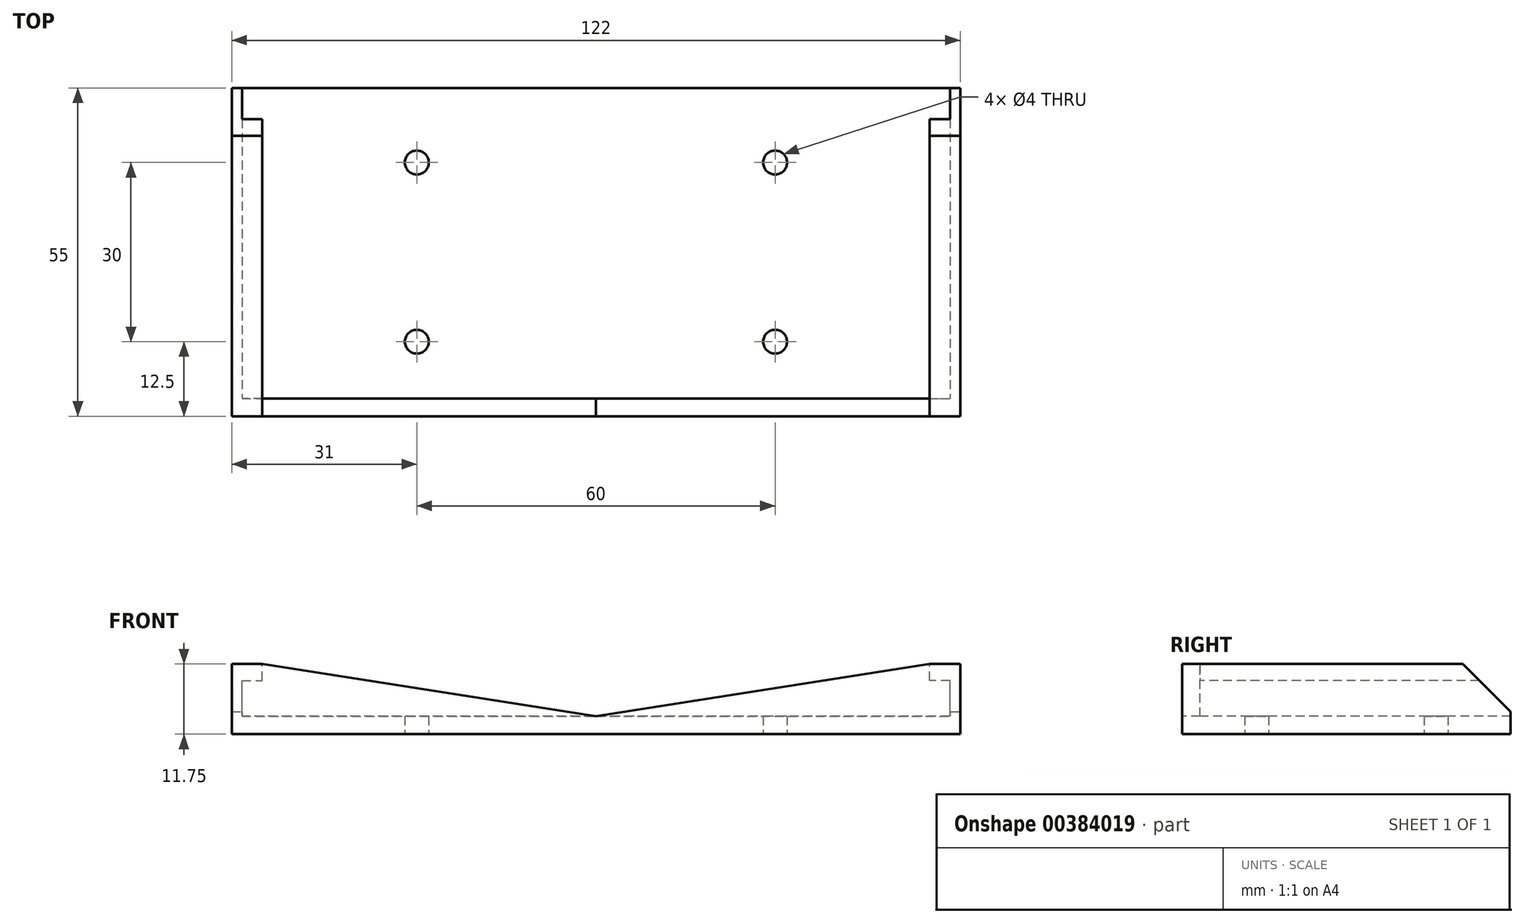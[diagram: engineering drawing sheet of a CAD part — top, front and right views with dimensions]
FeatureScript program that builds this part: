
annotation { "Feature Type Name" : "Feature", "Feature Type Description" : "" }
export const myFeature = defineFeature(function(context is Context, id is Id, definition is map)
    precondition{}
    {
        {
            var Q0;
            Q0=qCreatedBy(makeId("Top.planeOp"),FACE);
            var sketch = newSketch(context, id + "F0", { "sketchPlane" : qUnion([Q0])});
            skLineSegment(sketch, "E0.bottom", {"start": v(60, -27.5) * mm, "end": v(-60, -27.5) * mm});
            skLineSegment(sketch, "E0.top", {"start": v(60, 27.5) * mm, "end": v(-60, 27.5) * mm});
            skLineSegment(sketch, "E0.left", {"start": v(60, -27.5) * mm, "end": v(60, 27.5) * mm});
            skLineSegment(sketch, "E0.right", {"start": v(-60, -27.5) * mm, "end": v(-60, 27.5) * mm});
            skPoint(sketch, "E0.middle", {"position": v(0, 0) * mm});
            skCircle(sketch, "E1", {"center": v(-30, 15) * mm, "radius": 2 * mm});
            skCircle(sketch, "E2", {"center": v(30, 15) * mm, "radius": 2 * mm});
            skCircle(sketch, "E3", {"center": v(30, -15) * mm, "radius": 2 * mm});
            skCircle(sketch, "E4", {"center": v(-30, -15) * mm, "radius": 2 * mm});
            skSolve(sketch);
        }
        {
            var Q0;
            Q0 = qSketchRegion(id + "F0", true);
            extrude(context, id + "F1", {"entities" : qUnion([Q0]), "depth" : 3 * mm});
        }
        {
            var Q0;
            Q0=makeQuery(id+"F1.opExtrude","CAP_FACE",FACE,{"disambiguationData":[OSD([sQuery(id+"F0.wireOp",EDGE,"E0.bottom"),sQuery(id+"F0.wireOp",EDGE,"E0.top"),sQuery(id+"F0.wireOp",EDGE,"E0.left"),sQuery(id+"F0.wireOp",EDGE,"E0.right"),sQuery(id+"F0.wireOp",EDGE,"E1"),sQuery(id+"F0.wireOp",EDGE,"E2"),sQuery(id+"F0.wireOp",EDGE,"E3"),sQuery(id+"F0.wireOp",EDGE,"E4")])],"isStart":false});
            var sketch = newSketch(context, id + "F2", { "sketchPlane" : qUnion([Q0])});
            skLineSegment(sketch, "E5", {"start": v(58.88, 27.5) * mm, "end": v(58.88, -27.5) * mm});
            skLineSegment(sketch, "E6", {"start": v(58.88, 27.5) * mm, "end": v(60, 27.5) * mm});
            skLineSegment(sketch, "E7", {"start": v(60, 27.5) * mm, "end": v(60, -27.5) * mm});
            skLineSegment(sketch, "E8", {"start": v(60, -27.5) * mm, "end": v(58.88, -27.5) * mm});
            skLineSegment(sketch, "E9.MirrorCS", {"start": v(-60, -27.5) * mm, "end": v(-58.88, -27.5) * mm});
            skLineSegment(sketch, "E10.MirrorCS", {"start": v(-58.88, 27.5) * mm, "end": v(-60, 27.5) * mm});
            skLineSegment(sketch, "E11.MirrorCS", {"start": v(-60, 27.5) * mm, "end": v(-60, -27.5) * mm});
            skLineSegment(sketch, "E12.MirrorCS", {"start": v(-58.88, 27.5) * mm, "end": v(-58.88, -27.5) * mm});
            skSolve(sketch);
        }
        {
            var Q0;
            Q0 = qSketchRegion(id + "F2", true);
            extrude(context, id + "F3", {"entities" : qUnion([Q0]), "operationType" : NewBodyOperationType.ADD, "depth" : 6 * mm});
        }
        {
            var Q0;
            Q0=makeQuery(id+"F3.boolean.opBoolean","MERGE",FACE,{"derivedFrom":[makeQuery(id+"F1.opExtrude","SWEPT_FACE",FACE,{"disambiguationData":[OSD([sQuery(id+"F0.wireOp",EDGE,"E0.bottom")])]}),makeQuery(id+"F3.opExtrude","SWEPT_FACE",FACE,{"disambiguationData":[OSD([sQuery(id+"F2.wireOp",EDGE,"E8")])]}),makeQuery(id+"F3.opExtrude","SWEPT_FACE",FACE,{"disambiguationData":[OSD([sQuery(id+"F2.wireOp",EDGE,"E9.MirrorCS")])]})]});
            var sketch = newSketch(context, id + "F4", { "sketchPlane" : qUnion([Q0])});
            skLineSegment(sketch, "E13", {"start": v(-58.88, 3) * mm, "end": v(-58.88, 9) * mm});
            skLineSegment(sketch, "E14", {"start": v(-58.88, 9) * mm, "end": v(-55.88, 9) * mm});
            skLineSegment(sketch, "E15", {"start": v(-55.88, 9) * mm, "end": v(-55.88, 11.75) * mm});
            skLineSegment(sketch, "E16", {"start": v(-55.88, 11.75) * mm, "end": v(-61.88, 11.75) * mm});
            skLineSegment(sketch, "E17", {"start": v(-61.88, 11.75) * mm, "end": v(-61.88, 0) * mm});
            skLineSegment(sketch, "E18", {"start": v(-61.88, 0) * mm, "end": v(-52.74, 0) * mm});
            skLineSegment(sketch, "E19", {"start": v(-52.74, 0) * mm, "end": v(-58.88, 3) * mm});
            skLineSegment(sketch, "E20.MirrorCS", {"start": v(55.88, 11.75) * mm, "end": v(61.88, 11.75) * mm});
            skLineSegment(sketch, "E21.MirrorCS", {"start": v(61.88, 11.75) * mm, "end": v(61.88, 0) * mm});
            skLineSegment(sketch, "E22.MirrorCS", {"start": v(61.88, 0) * mm, "end": v(52.74, 0) * mm});
            skLineSegment(sketch, "E23.MirrorCS", {"start": v(58.88, 3) * mm, "end": v(58.88, 9) * mm});
            skLineSegment(sketch, "E24.MirrorCS", {"start": v(55.88, 9) * mm, "end": v(55.88, 11.75) * mm});
            skLineSegment(sketch, "E25.MirrorCS", {"start": v(52.74, 0) * mm, "end": v(58.88, 3) * mm});
            skLineSegment(sketch, "E26.MirrorCS", {"start": v(58.88, 9) * mm, "end": v(55.88, 9) * mm});
            skSolve(sketch);
        }
        {
            var Q0;
            Q0 = qSketchRegion(id + "F4", true);
            extrude(context, id + "F5", {"entities" : qUnion([Q0]), "operationType" : NewBodyOperationType.ADD, "oppositeDirection" : true, "depth" : 55 * mm});
        }
        {
            var Q0;
            Q0=makeQuery(id+"F5.boolean.opBoolean","MERGE",FACE,{"derivedFrom":[makeQuery(id+"F3.boolean.opBoolean","MERGE",FACE,{"derivedFrom":[makeQuery(id+"F1.opExtrude","SWEPT_FACE",FACE,{"disambiguationData":[OSD([sQuery(id+"F0.wireOp",EDGE,"E0.bottom")])]}),makeQuery(id+"F3.opExtrude","SWEPT_FACE",FACE,{"disambiguationData":[OSD([sQuery(id+"F2.wireOp",EDGE,"E8")])]}),makeQuery(id+"F3.opExtrude","SWEPT_FACE",FACE,{"disambiguationData":[OSD([sQuery(id+"F2.wireOp",EDGE,"E9.MirrorCS")])]})]}),makeQuery(id+"F5.opExtrude","CAP_FACE",FACE,{"disambiguationData":[OSD([sQuery(id+"F4.wireOp",EDGE,"E13"),sQuery(id+"F4.wireOp",EDGE,"E14"),sQuery(id+"F4.wireOp",EDGE,"E15"),sQuery(id+"F4.wireOp",EDGE,"E16"),sQuery(id+"F4.wireOp",EDGE,"E17"),sQuery(id+"F4.wireOp",EDGE,"E18"),sQuery(id+"F4.wireOp",EDGE,"E19")])],"isStart":true}),makeQuery(id+"F5.opExtrude","CAP_FACE",FACE,{"disambiguationData":[OSD([sQuery(id+"F4.wireOp",EDGE,"E20.MirrorCS"),sQuery(id+"F4.wireOp",EDGE,"E21.MirrorCS"),sQuery(id+"F4.wireOp",EDGE,"E22.MirrorCS"),sQuery(id+"F4.wireOp",EDGE,"E23.MirrorCS"),sQuery(id+"F4.wireOp",EDGE,"E24.MirrorCS"),sQuery(id+"F4.wireOp",EDGE,"E25.MirrorCS"),sQuery(id+"F4.wireOp",EDGE,"E26.MirrorCS")])],"isStart":true})]});
            var sketch = newSketch(context, id + "F6", { "sketchPlane" : qUnion([Q0])});
            skLineSegment(sketch, "E27", {"start": v(-58.88, 9) * mm, "end": v(-59.27, 9) * mm});
            skLineSegment(sketch, "E28", {"start": v(-59.27, 9) * mm, "end": v(-59.27, 3) * mm});
            skLineSegment(sketch, "E29", {"start": v(-59.27, 3) * mm, "end": v(-58.88, 3) * mm});
            skLineSegment(sketch, "E30.MirrorCS", {"start": v(59.27, 3) * mm, "end": v(58.88, 3) * mm});
            skLineSegment(sketch, "E31.MirrorCS", {"start": v(59.27, 9) * mm, "end": v(59.27, 3) * mm});
            skLineSegment(sketch, "E32.MirrorCS", {"start": v(58.88, 9) * mm, "end": v(59.27, 9) * mm});
            skSolve(sketch);
        }
        {
            var Q0;
            Q0=makeQuery(id+"F6.imprint","IMPRINT",FACE,{"disambiguationData":[TD([[makeQuery(id+"F6.imprint","IMPRINT",EDGE,{"derivedFrom":sQuery(id+"F6.wireOp",EDGE,"E27")}),1.0]])]});
            var Q1;
            Q1=makeQuery(id+"F6.imprint","IMPRINT",FACE,{"disambiguationData":[TD([[makeQuery(id+"F6.imprint","IMPRINT",EDGE,{"derivedFrom":sQuery(id+"F6.wireOp",EDGE,"E30.MirrorCS")}),-1.0]])]});
            extrude(context, id + "F7", {"entities" : qUnion([Q0, Q1]), "operationType" : NewBodyOperationType.REMOVE, "oppositeDirection" : true, "depth" : 56.2 * mm});
        }
        {
            var Q0;
            Q0=makeQuery(id+"F5.boolean.opBoolean","MERGE",FACE,{"derivedFrom":[makeQuery(id+"F3.boolean.opBoolean","MERGE",FACE,{"derivedFrom":[makeQuery(id+"F1.opExtrude","SWEPT_FACE",FACE,{"disambiguationData":[OSD([sQuery(id+"F0.wireOp",EDGE,"E0.bottom")])]}),makeQuery(id+"F3.opExtrude","SWEPT_FACE",FACE,{"disambiguationData":[OSD([sQuery(id+"F2.wireOp",EDGE,"E8")])]}),makeQuery(id+"F3.opExtrude","SWEPT_FACE",FACE,{"disambiguationData":[OSD([sQuery(id+"F2.wireOp",EDGE,"E9.MirrorCS")])]})]}),makeQuery(id+"F5.opExtrude","CAP_FACE",FACE,{"disambiguationData":[OSD([sQuery(id+"F4.wireOp",EDGE,"E13"),sQuery(id+"F4.wireOp",EDGE,"E14"),sQuery(id+"F4.wireOp",EDGE,"E15"),sQuery(id+"F4.wireOp",EDGE,"E16"),sQuery(id+"F4.wireOp",EDGE,"E17"),sQuery(id+"F4.wireOp",EDGE,"E18"),sQuery(id+"F4.wireOp",EDGE,"E19")])],"isStart":true}),makeQuery(id+"F5.opExtrude","CAP_FACE",FACE,{"disambiguationData":[OSD([sQuery(id+"F4.wireOp",EDGE,"E20.MirrorCS"),sQuery(id+"F4.wireOp",EDGE,"E21.MirrorCS"),sQuery(id+"F4.wireOp",EDGE,"E22.MirrorCS"),sQuery(id+"F4.wireOp",EDGE,"E23.MirrorCS"),sQuery(id+"F4.wireOp",EDGE,"E24.MirrorCS"),sQuery(id+"F4.wireOp",EDGE,"E25.MirrorCS"),sQuery(id+"F4.wireOp",EDGE,"E26.MirrorCS")])],"isStart":true})]});
            var sketch = newSketch(context, id + "F8", { "sketchPlane" : qUnion([Q0])});
            skLineSegment(sketch, "E33", {"start": v(-55.88, 11.75) * mm, "end": v(0, 3) * mm});
            skLineSegment(sketch, "E34", {"start": v(0, 3) * mm, "end": v(55.88, 11.75) * mm});
            skLineSegment(sketch, "E35", {"start": v(55.88, 11.75) * mm, "end": v(61.88, 11.75) * mm});
            skLineSegment(sketch, "E36", {"start": v(61.88, 11.75) * mm, "end": v(61.88, 0) * mm});
            skLineSegment(sketch, "E37", {"start": v(61.88, 0) * mm, "end": v(-61.88, 0) * mm});
            skLineSegment(sketch, "E38", {"start": v(-61.88, 0) * mm, "end": v(-61.88, 11.75) * mm});
            skLineSegment(sketch, "E39", {"start": v(-61.88, 11.75) * mm, "end": v(-55.88, 11.75) * mm});
            skSolve(sketch);
        }
        {
            var Q0;
            Q0 = qSketchRegion(id + "F8", true);
            extrude(context, id + "F9", {"entities" : qUnion([Q0]), "operationType" : NewBodyOperationType.ADD, "oppositeDirection" : true, "depth" : 3 * mm});
        }
        {
            var Q0;
            Q0=makeQuery(id+"F5.opExtrude","CAP_EDGE",EDGE,{"disambiguationData":[OSD([sQuery(id+"F4.wireOp",EDGE,"E20.MirrorCS")])],"isStart":false});
            var Q1;
            Q1=makeQuery(id+"F5.opExtrude","CAP_EDGE",EDGE,{"disambiguationData":[OSD([sQuery(id+"F4.wireOp",EDGE,"E16")])],"isStart":false});
            chamfer(context, id + "F10", {"entities" : qUnion([Q0, Q1]), "width" : 8 * mm, "tangentPropagation" : true});
        }
        {
            var Q0;
            Q0=makeQuery(id+"F7.boolean.opBoolean","MERGE",FACE,{"derivedFrom":[makeQuery(id+"F1.opExtrude","CAP_FACE",FACE,{"disambiguationData":[OSD([sQuery(id+"F0.wireOp",EDGE,"E0.bottom"),sQuery(id+"F0.wireOp",EDGE,"E0.top"),sQuery(id+"F0.wireOp",EDGE,"E0.left"),sQuery(id+"F0.wireOp",EDGE,"E0.right"),sQuery(id+"F0.wireOp",EDGE,"E1"),sQuery(id+"F0.wireOp",EDGE,"E2"),sQuery(id+"F0.wireOp",EDGE,"E3"),sQuery(id+"F0.wireOp",EDGE,"E4")])],"isStart":false}),makeQuery(id+"F7.opExtrude","SWEPT_FACE",FACE,{"disambiguationData":[OSD([sQuery(id+"F6.wireOp",EDGE,"E29")])]}),makeQuery(id+"F7.opExtrude","SWEPT_FACE",FACE,{"disambiguationData":[OSD([sQuery(id+"F6.wireOp",EDGE,"E30.MirrorCS")])]})]});
            var sketch = newSketch(context, id + "F11", { "sketchPlane" : qUnion([Q0])});
            skLineSegment(sketch, "E40.bottom", {"start": v(-61, 32.7) * mm, "end": v(-70.09, 32.7) * mm});
            skLineSegment(sketch, "E40.top", {"start": v(-61, -34.61) * mm, "end": v(-70.09, -34.61) * mm});
            skLineSegment(sketch, "E40.left", {"start": v(-61, 32.7) * mm, "end": v(-61, -34.61) * mm});
            skLineSegment(sketch, "E40.right", {"start": v(-70.09, 32.7) * mm, "end": v(-70.09, -34.61) * mm});
            skLineSegment(sketch, "E41.bottom", {"start": v(61, 33.2) * mm, "end": v(73.62, 33.2) * mm});
            skLineSegment(sketch, "E41.top", {"start": v(61, -35.96) * mm, "end": v(73.62, -35.96) * mm});
            skLineSegment(sketch, "E41.left", {"start": v(61, 33.2) * mm, "end": v(61, -35.96) * mm});
            skLineSegment(sketch, "E41.right", {"start": v(73.62, 33.2) * mm, "end": v(73.62, -35.96) * mm});
            skSolve(sketch);
        }
        {
            var Q0;
            Q0 = qSketchRegion(id + "F11", true);
            extrude(context, id + "F12", {"entities" : qUnion([Q0]), "operationType" : NewBodyOperationType.REMOVE, "endBound" : BoundingType.SYMMETRIC, "oppositeDirection" : true, "depth" : 25 * mm});
        }
    });
